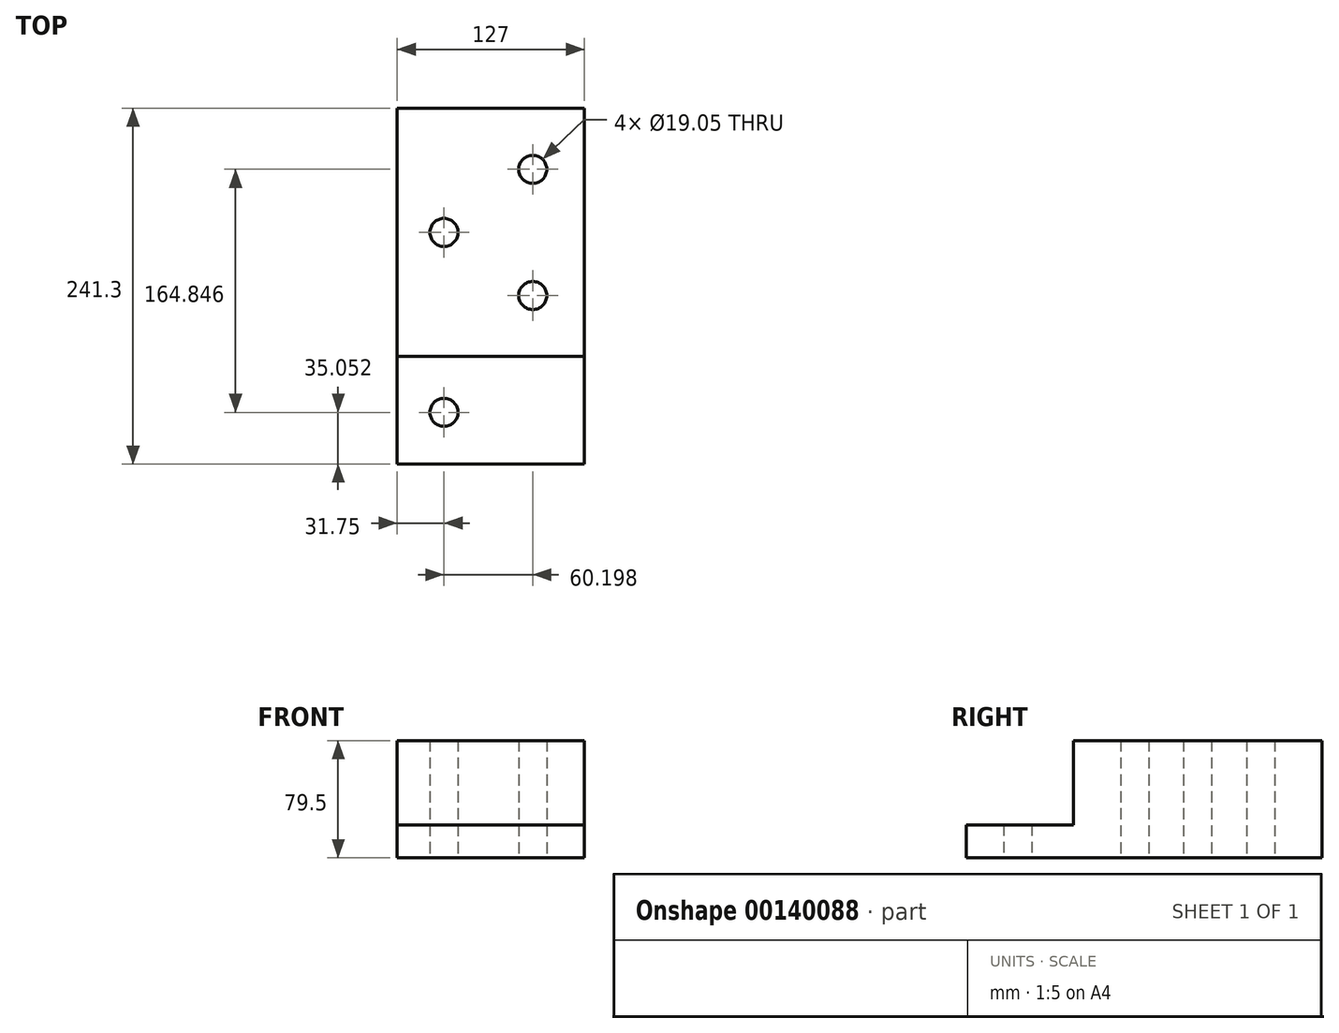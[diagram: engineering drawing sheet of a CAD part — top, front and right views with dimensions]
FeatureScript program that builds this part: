
annotation { "Feature Type Name" : "Feature", "Feature Type Description" : "" }
export const myFeature = defineFeature(function(context is Context, id is Id, definition is map)
    precondition{}
    {
        {
            var Q0;
            Q0=qCreatedBy(makeId("Top.planeOp"),FACE);
            var sketch = newSketch(context, id + "F0", { "sketchPlane" : qUnion([Q0])});
            skLineSegment(sketch, "E0.bottom", {"start": v(0, 0) * mm, "end": v(127, 0) * mm});
            skLineSegment(sketch, "E0.top", {"start": v(0, 241.3) * mm, "end": v(127, 241.3) * mm});
            skLineSegment(sketch, "E0.left", {"start": v(0, 0) * mm, "end": v(0, 241.3) * mm});
            skLineSegment(sketch, "E0.right", {"start": v(127, 0) * mm, "end": v(127, 241.3) * mm});
            skLineSegment(sketch, "E1", {"start": v(0, 72.9) * mm, "end": v(127, 72.9) * mm});
            skLineSegment(sketch, "E2", {"start": v(91.95, 241.3) * mm, "end": v(91.95, 72.9) * mm, "construction": true});
            skLineSegment(sketch, "E3", {"start": v(31.75, 241.3) * mm, "end": v(31.75, 72.9) * mm, "construction": true});
            skCircle(sketch, "E4", {"center": v(91.95, 199.9) * mm, "radius": 9.53 * mm});
            skCircle(sketch, "E5", {"center": v(91.95, 114.3) * mm, "radius": 9.53 * mm});
            skCircle(sketch, "E6", {"center": v(31.75, 157.1) * mm, "radius": 9.53 * mm});
            skLineSegment(sketch, "E7", {"start": v(31.75, 72.9) * mm, "end": v(31.75, 0) * mm, "construction": true});
            skLineSegment(sketch, "E8", {"start": v(0, 35.05) * mm, "end": v(63.5, 35.05) * mm, "construction": true});
            skCircle(sketch, "E9", {"center": v(31.75, 35.05) * mm, "radius": 9.53 * mm});
            skPoint(sketch, "E9.centerSnap0", {"position": v(31.75, 35.05) * mm});
            skSolve(sketch);
        }
        {
            var Q0;
            Q0 = qSketchRegion(id + "F0", true);
            extrude(context, id + "F1", {"entities" : qUnion([Q0]), "depth" : 79.5 * mm});
        }
        {
            var Q0;
            Q0=makeQuery(id+"F1.opExtrude","CAP_FACE",FACE,{"disambiguationData":[OSD([sQuery(id+"F0.wireOp",EDGE,"E0.bottom"),sQuery(id+"F0.wireOp",EDGE,"E0.top"),sQuery(id+"F0.wireOp",EDGE,"E0.left"),sQuery(id+"F0.wireOp",EDGE,"E0.right"),sQuery(id+"F0.wireOp",EDGE,"E4"),sQuery(id+"F0.wireOp",EDGE,"E5"),sQuery(id+"F0.wireOp",EDGE,"E6"),sQuery(id+"F0.wireOp",EDGE,"E9")])],"isStart":false});
            var sketch = newSketch(context, id + "F2", { "sketchPlane" : qUnion([Q0])});
            skLineSegment(sketch, "E10.bottom", {"start": v(0, 0) * mm, "end": v(127, 0) * mm});
            skLineSegment(sketch, "E10.top", {"start": v(0, 72.9) * mm, "end": v(127, 72.9) * mm});
            skLineSegment(sketch, "E10.left", {"start": v(0, 0) * mm, "end": v(0, 72.9) * mm});
            skLineSegment(sketch, "E10.right", {"start": v(127, 0) * mm, "end": v(127, 72.9) * mm});
            skSolve(sketch);
        }
        {
            var Q0;
            Q0 = qSketchRegion(id + "F2", true);
            extrude(context, id + "F3", {"entities" : qUnion([Q0]), "operationType" : NewBodyOperationType.REMOVE, "oppositeDirection" : true, "depth" : 57.15 * mm});
        }
    });
